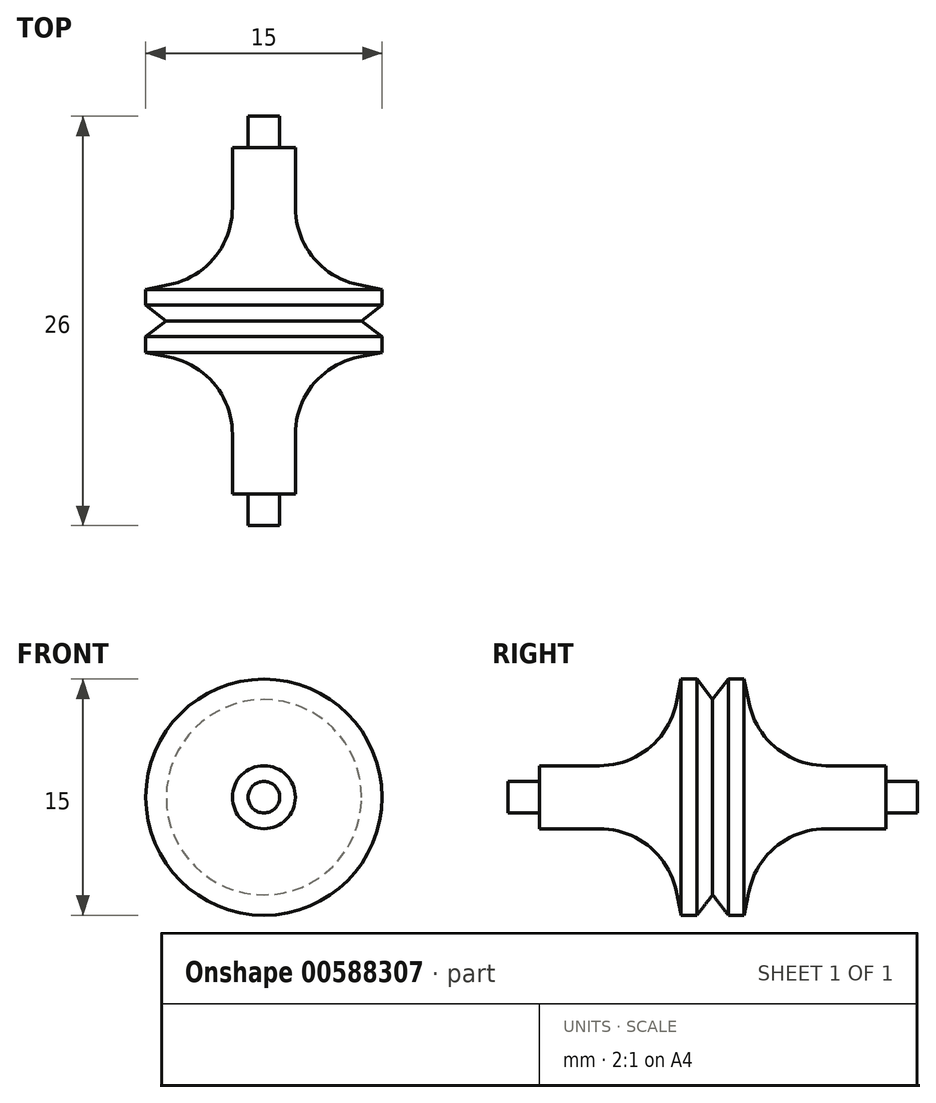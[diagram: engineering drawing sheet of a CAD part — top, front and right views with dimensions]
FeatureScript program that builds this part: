
annotation { "Feature Type Name" : "Feature", "Feature Type Description" : "" }
export const myFeature = defineFeature(function(context is Context, id is Id, definition is map)
    precondition{}
    {
        {
            var Q0;
            Q0=qCreatedBy(makeId("Right.planeOp"),FACE);
            var sketch = newSketch(context, id + "F0", { "sketchPlane" : qUnion([Q0])});
            skLineSegment(sketch, "E0", {"start": v(-95.37, 9.25) * mm, "end": v(90.17, 9.25) * mm, "construction": true});
            skLineSegment(sketch, "E1", {"start": v(-26, 63) * mm, "end": v(-26, -43.93) * mm, "construction": true});
            skLineSegment(sketch, "E2", {"start": v(-26, 9.25) * mm, "end": v(-13, 9.25) * mm});
            skLineSegment(sketch, "E3", {"start": v(-13, 9.25) * mm, "end": v(-13, 10.25) * mm});
            skLineSegment(sketch, "E4", {"start": v(-13, 10.25) * mm, "end": v(-15, 10.25) * mm});
            skLineSegment(sketch, "E5", {"start": v(-15, 10.25) * mm, "end": v(-15, 11.25) * mm});
            skLineSegment(sketch, "E6", {"start": v(-15, 11.25) * mm, "end": v(-22.9, 11.25) * mm});
            skLineSegment(sketch, "E7", {"start": v(-25, 16.75) * mm, "end": v(-24, 16.75) * mm});
            skLineSegment(sketch, "E8", {"start": v(-24, 16.75) * mm, "end": v(-22.9, 11.25) * mm});
            skLineSegment(sketch, "E9", {"start": v(-25, 16.75) * mm, "end": v(-26, 15.45) * mm});
            skPoint(sketch, "E10.orphan", {"position": v(-26, 16.75) * mm});
            skLineSegment(sketch, "E11.MirrorCS", {"start": v(-26, 9.25) * mm, "end": v(-39, 9.25) * mm});
            skLineSegment(sketch, "E12.MirrorCS", {"start": v(-39, 10.25) * mm, "end": v(-37, 10.25) * mm});
            skLineSegment(sketch, "E13.MirrorCS", {"start": v(-37, 10.25) * mm, "end": v(-37, 11.25) * mm});
            skLineSegment(sketch, "E14.MirrorCS", {"start": v(-37, 11.25) * mm, "end": v(-29.11, 11.25) * mm});
            skLineSegment(sketch, "E15.MirrorCS", {"start": v(-28, 16.75) * mm, "end": v(-29.11, 11.25) * mm});
            skLineSegment(sketch, "E16.MirrorCS", {"start": v(-27, 16.75) * mm, "end": v(-28, 16.75) * mm});
            skLineSegment(sketch, "E17.MirrorCS", {"start": v(-27, 16.75) * mm, "end": v(-26, 15.45) * mm});
            skLineSegment(sketch, "E18", {"start": v(-39, 10.25) * mm, "end": v(-39, 9.25) * mm});
            skSolve(sketch);
        }
        {
            var Q0;
            Q0=makeQuery(id+"F0.imprint","IMPRINT",FACE,{"disambiguationData":[TD([[makeQuery(id+"F0.imprint","IMPRINT",EDGE,{"derivedFrom":sQuery(id+"F0.wireOp",EDGE,"E2")}),1.0]])]});
            var Q1;
            Q1=sQuery(id+"F0.wireOp",EDGE,"E2");
            revolve(context, id + "F1", {"entities" : qUnion([Q0]), "axis" : qUnion([Q1]), "revolveType" : RevolveType.FULL});
        }
        {
            var Q0;
            Q0=makeQuery(id+"F1.opRevolve","SWEPT_EDGE",EDGE,{"disambiguationData":[OSD([sQuery(id+"F0.wireOp",EDGE,"E14.MirrorCS"),sQuery(id+"F0.wireOp",EDGE,"E15.MirrorCS")])]});
            fillet(context, id + "F2", {"entities" : qUnion([Q0]), "radius" : 5 * mm, "tangentPropagation" : true, "allowEdgeOverflow" : false});
        }
        {
            var Q0;
            Q0=makeQuery(id+"F1.opRevolve","SWEPT_EDGE",EDGE,{"disambiguationData":[OSD([sQuery(id+"F0.wireOp",EDGE,"E6"),sQuery(id+"F0.wireOp",EDGE,"E8")])]});
            fillet(context, id + "F3", {"entities" : qUnion([Q0]), "radius" : 5 * mm, "tangentPropagation" : true, "allowEdgeOverflow" : false});
        }
    });
